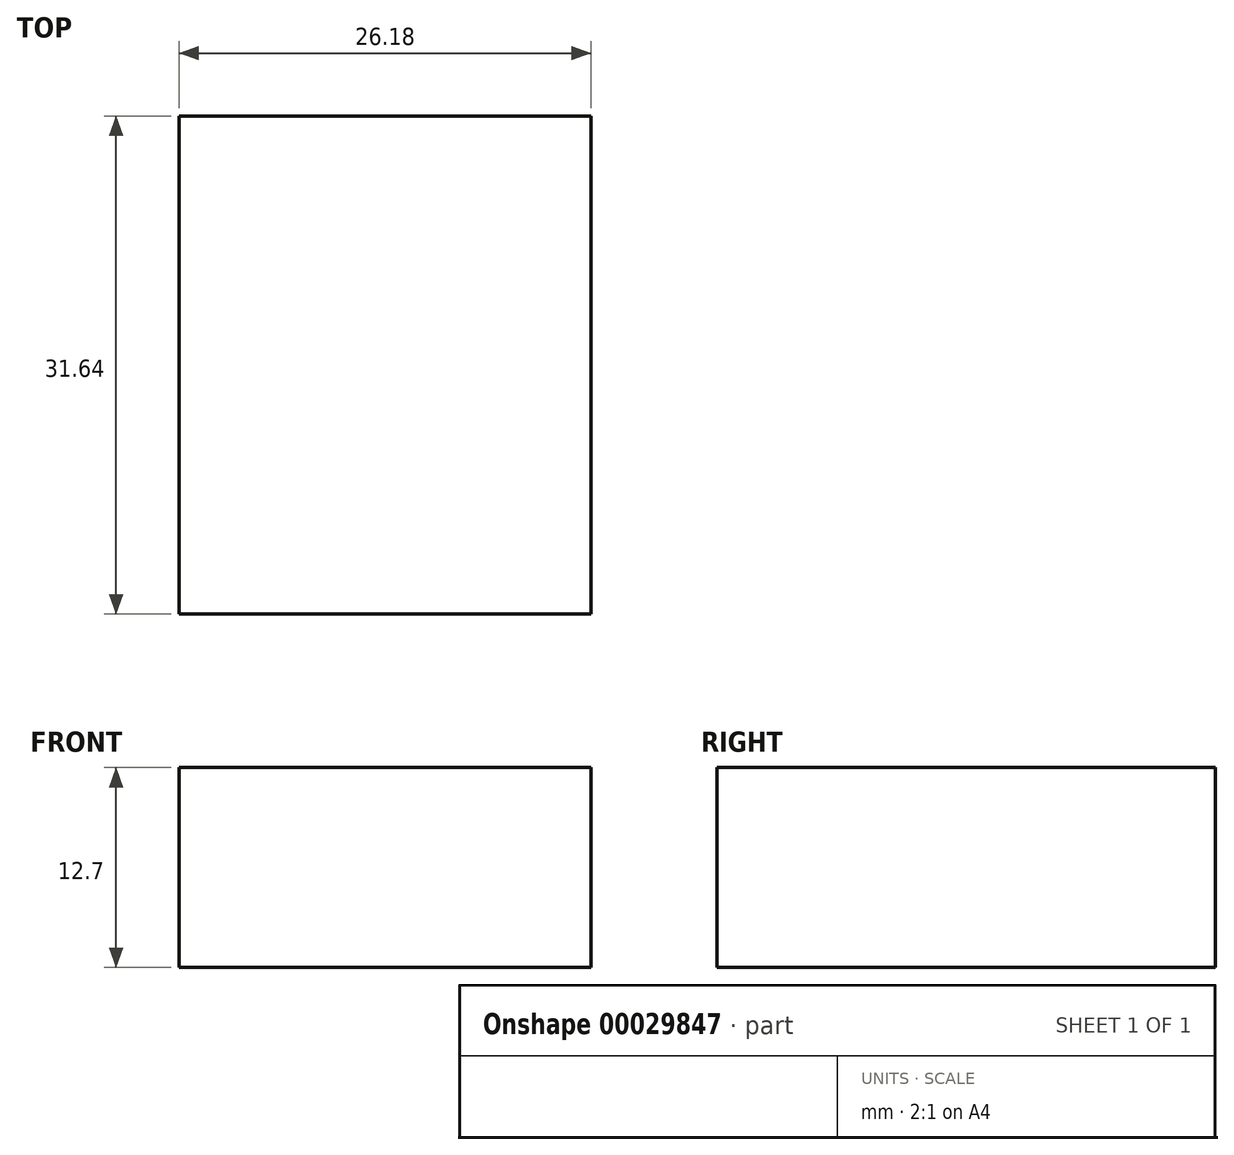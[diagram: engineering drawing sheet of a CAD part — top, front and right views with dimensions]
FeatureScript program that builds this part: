
annotation { "Feature Type Name" : "Feature", "Feature Type Description" : "" }
export const myFeature = defineFeature(function(context is Context, id is Id, definition is map)
    precondition{}
    {
        {
            var Q0;
            Q0=qCreatedBy(makeId("Top.planeOp"),FACE);
            var sketch = newSketch(context, id + "F0", { "sketchPlane" : qUnion([Q0])});
            skLineSegment(sketch, "E0.bottom", {"start": v(0, 0) * mm, "end": v(26.18, 0) * mm});
            skLineSegment(sketch, "E0.top", {"start": v(0, 31.64) * mm, "end": v(26.18, 31.64) * mm});
            skLineSegment(sketch, "E0.left", {"start": v(0, 0) * mm, "end": v(0, 31.64) * mm});
            skLineSegment(sketch, "E0.right", {"start": v(26.18, 0) * mm, "end": v(26.18, 31.64) * mm});
            skSolve(sketch);
        }
        {
            var Q0;
            Q0 = qSketchRegion(id + "F0", true);
            extrude(context, id + "F1", {"entities" : qUnion([Q0]), "depth" : 12.7 * mm});
        }
    });
